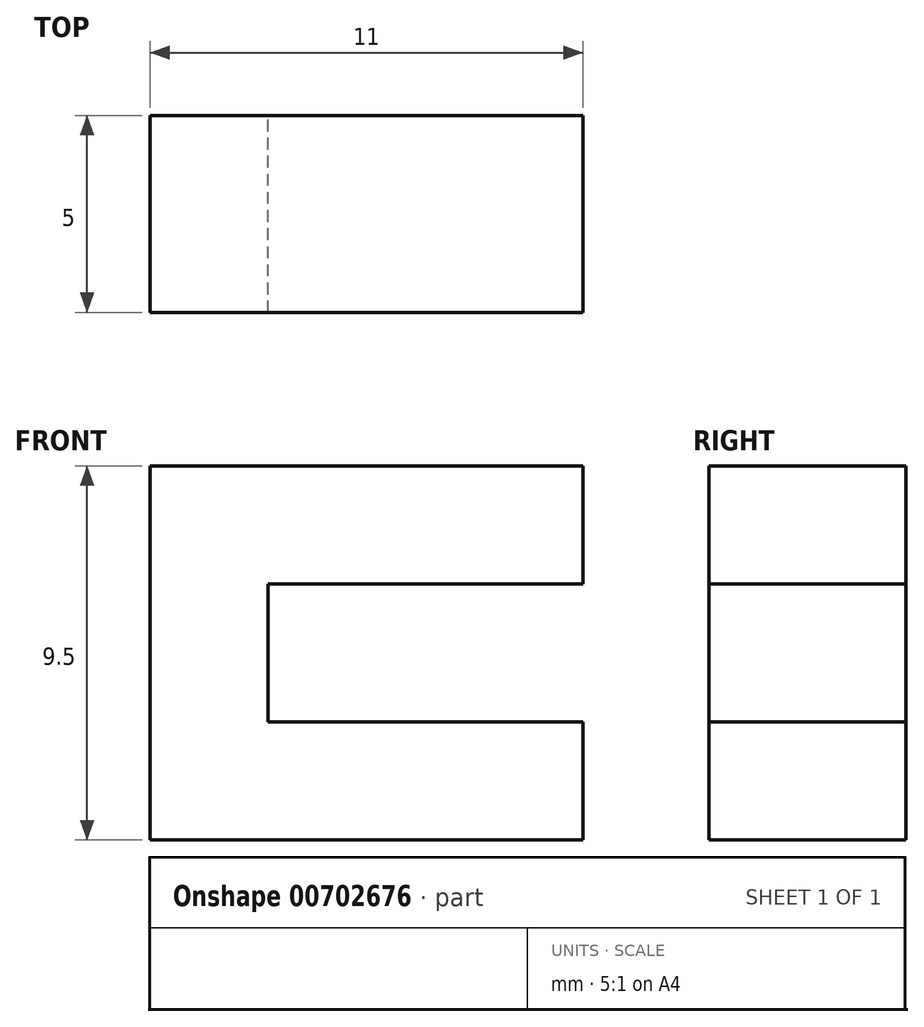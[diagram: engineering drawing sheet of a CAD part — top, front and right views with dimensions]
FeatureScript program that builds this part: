
annotation { "Feature Type Name" : "Feature", "Feature Type Description" : "" }
export const myFeature = defineFeature(function(context is Context, id is Id, definition is map)
    precondition{}
    {
        {
            var Q0;
            Q0=qCreatedBy(makeId("Front.planeOp"),FACE);
            var sketch = newSketch(context, id + "F0", { "sketchPlane" : qUnion([Q0])});
            skLineSegment(sketch, "E0", {"start": v(0, 0) * mm, "end": v(-11, 0) * mm});
            skLineSegment(sketch, "E1", {"start": v(-11, 9.5) * mm, "end": v(-11, 0) * mm});
            skLineSegment(sketch, "E2", {"start": v(-11, 9.5) * mm, "end": v(0, 9.5) * mm});
            skLineSegment(sketch, "E3.0", {"start": v(-8, 6.5) * mm, "end": v(0, 6.5) * mm});
            skLineSegment(sketch, "E3.1", {"start": v(-8, 6.5) * mm, "end": v(-8, 3) * mm});
            skLineSegment(sketch, "E3.2", {"start": v(0, 3) * mm, "end": v(-8, 3) * mm});
            skLineSegment(sketch, "E4", {"start": v(0, 6.5) * mm, "end": v(0, 9.5) * mm});
            skLineSegment(sketch, "E5", {"start": v(0, 3) * mm, "end": v(0, 0) * mm});
            skSolve(sketch);
        }
        {
            var Q0;
            Q0 = qSketchRegion(id + "F0", true);
            extrude(context, id + "F1", {"entities" : qUnion([Q0]), "endBound" : BoundingType.SYMMETRIC, "depth" : 5 * mm, "offsetDistance" : 25 * mm});
        }
    });
